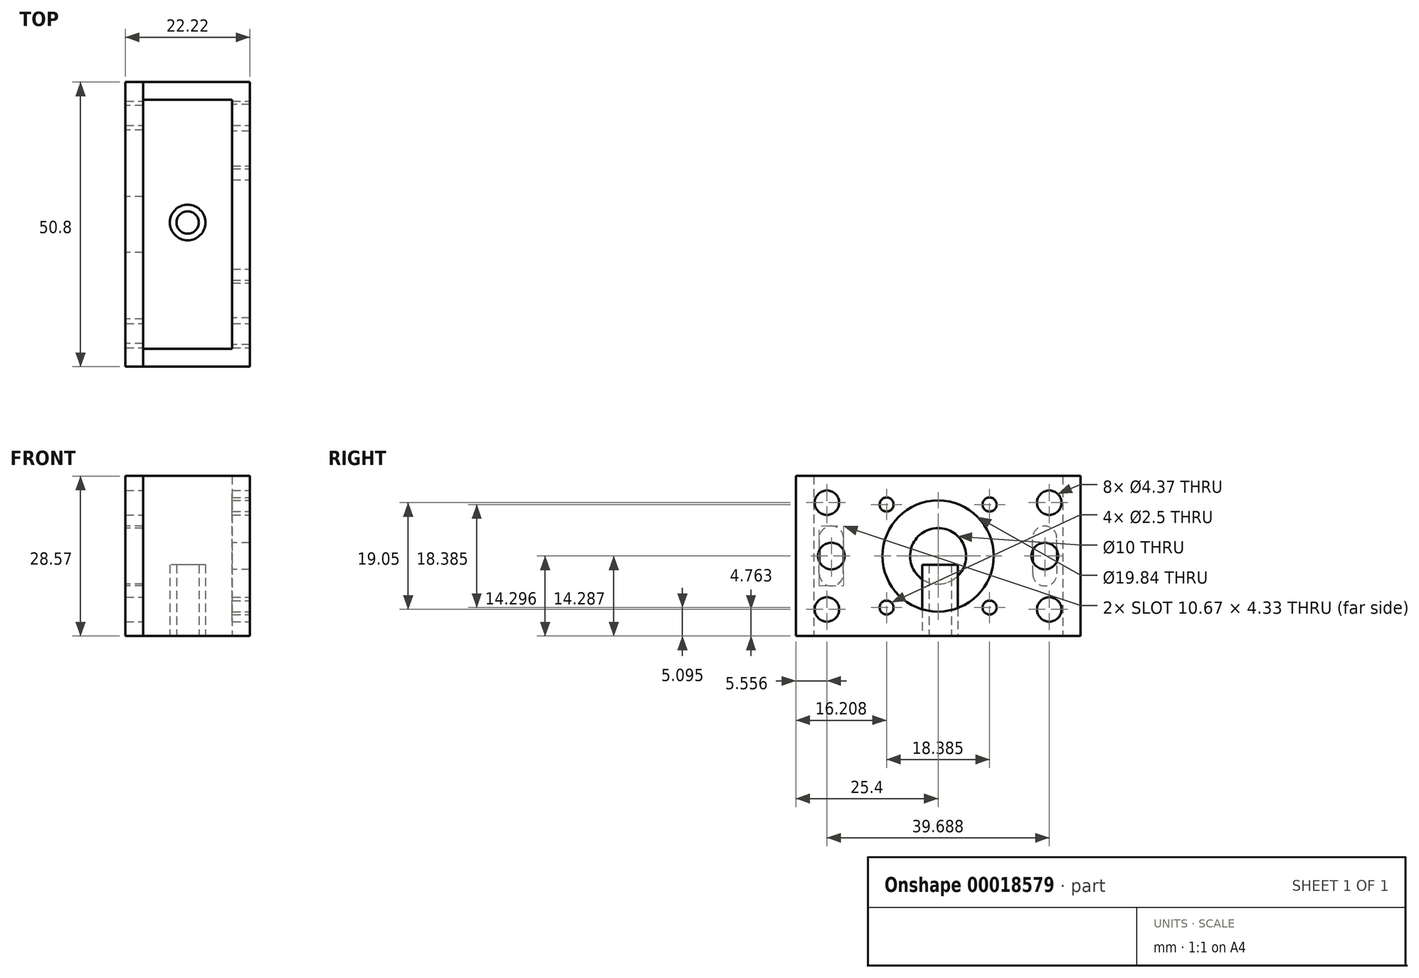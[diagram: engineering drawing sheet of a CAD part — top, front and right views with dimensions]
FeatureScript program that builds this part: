
annotation { "Feature Type Name" : "Feature", "Feature Type Description" : "" }
export const myFeature = defineFeature(function(context is Context, id is Id, definition is map)
    precondition{}
    {
        {
            var Q0;
            Q0=qCreatedBy(makeId("Top.planeOp"),FACE);
            var sketch = newSketch(context, id + "F0", { "sketchPlane" : qUnion([Q0])});
            skCircle(sketch, "E0", {"center": v(0, 0.35) * mm, "radius": 3.18 * mm});
            skCircle(sketch, "E1", {"center": v(0, 0.35) * mm, "radius": 2 * mm});
            skSolve(sketch);
        }
        {
            var Q0;
            Q0 = qSketchRegion(id + "F0", true);
            extrude(context, id + "F1", {"entities" : qUnion([Q0]), "depth" : 12.7 * mm});
        }
        {
            var Q0;
            Q0=qCreatedBy(makeId("Top.planeOp"),FACE);
            var sketch = newSketch(context, id + "F2", { "sketchPlane" : qUnion([Q0])});
            skLineSegment(sketch, "E2.rect.bottom", {"start": v(7.94, 22.22) * mm, "end": v(-7.94, 22.22) * mm});
            skLineSegment(sketch, "E2.rect.top", {"start": v(7.94, -22.22) * mm, "end": v(-7.94, -22.22) * mm});
            skLineSegment(sketch, "E2.rect.left", {"start": v(7.94, 22.22) * mm, "end": v(7.94, -22.23) * mm});
            skPoint(sketch, "E2.rect.middle", {"position": v(0, 0) * mm});
            skLineSegment(sketch, "E3.0", {"start": v(11.11, 25.4) * mm, "end": v(-7.94, 25.4) * mm});
            skLineSegment(sketch, "E3.1", {"start": v(11.11, 25.4) * mm, "end": v(11.11, -25.4) * mm});
            skLineSegment(sketch, "E3.2", {"start": v(11.11, -25.4) * mm, "end": v(-7.94, -25.4) * mm});
            skLineSegment(sketch, "E4", {"start": v(-7.94, 22.22) * mm, "end": v(-7.94, 25.4) * mm});
            skLineSegment(sketch, "E5", {"start": v(-7.94, -22.22) * mm, "end": v(-7.94, -25.4) * mm});
            skSolve(sketch);
        }
        {
            var Q0;
            Q0 = qSketchRegion(id + "F2", true);
            extrude(context, id + "F3", {"entities" : qUnion([Q0]), "depth" : 28.57 * mm});
        }
        {
            var Q0;
            Q0=makeQuery(id+"F3.opExtrude","SWEPT_FACE",FACE,{"disambiguationData":[OSD([sQuery(id+"F2.wireOp",EDGE,"E3.1")])]});
            var sketch = newSketch(context, id + "F4", { "sketchPlane" : qUnion([Q0])});
            skLineSegment(sketch, "E6", {"start": v(25.4, 14.29) * mm, "end": v(-25.4, 14.29) * mm, "construction": true});
            skLineSegment(sketch, "E7", {"start": v(0, 28.58) * mm, "end": v(0, 0) * mm, "construction": true});
            skCircle(sketch, "E8", {"center": v(0, 14.29) * mm, "radius": 9.92 * mm});
            skCircle(sketch, "E9", {"center": v(0, 14.29) * mm, "radius": 13 * mm, "construction": true});
            skCircle(sketch, "E10", {"center": v(9.2, 23.48) * mm, "radius": 1.25 * mm});
            skLineSegment(sketch, "E11", {"start": v(9.2, 23.48) * mm, "end": v(0, 14.29) * mm, "construction": true});
            skCircle(sketch, "E12.1.0", {"center": v(-9.2, 23.48) * mm, "radius": 1.25 * mm});
            skCircle(sketch, "E12.2.0", {"center": v(-9.2, 5.1) * mm, "radius": 1.25 * mm});
            skCircle(sketch, "E12.3.0", {"center": v(9.2, 5.1) * mm, "radius": 1.25 * mm});
            skSolve(sketch);
        }
        {
            var Q0;
            Q0 = qSketchRegion(id + "F4", true);
            extrude(context, id + "F5", {"entities" : qUnion([Q0]), "operationType" : NewBodyOperationType.REMOVE, "endBound" : BoundingType.UP_TO_NEXT, "oppositeDirection" : true, "depth" : 25 * mm});
        }
        {
            var Q0;
            Q0=qCreatedBy(makeId("Top.planeOp"),FACE);
            var sketch = newSketch(context, id + "F6", { "sketchPlane" : qUnion([Q0])});
            skLineSegment(sketch, "E13.bottom", {"start": v(-7.94, 25.4) * mm, "end": v(-11.11, 25.4) * mm});
            skLineSegment(sketch, "E13.top", {"start": v(-7.94, -25.4) * mm, "end": v(-11.11, -25.4) * mm});
            skLineSegment(sketch, "E13.left", {"start": v(-7.94, 25.4) * mm, "end": v(-7.94, -25.4) * mm});
            skLineSegment(sketch, "E13.right", {"start": v(-11.11, 25.4) * mm, "end": v(-11.11, -25.4) * mm});
            skSolve(sketch);
        }
        {
            var Q0;
            Q0 = qSketchRegion(id + "F6", true);
            var Q1;
            Q1=makeQuery(id+"F3.opExtrude","CAP_FACE",FACE,{"disambiguationData":[OSD([sQuery(id+"F2.wireOp",EDGE,"E2.rect.bottom"),sQuery(id+"F2.wireOp",EDGE,"E2.rect.top"),sQuery(id+"F2.wireOp",EDGE,"E2.rect.left"),sQuery(id+"F2.wireOp",EDGE,"E3.0"),sQuery(id+"F2.wireOp",EDGE,"E3.1"),sQuery(id+"F2.wireOp",EDGE,"E3.2"),sQuery(id+"F2.wireOp",EDGE,"E4"),sQuery(id+"F2.wireOp",EDGE,"E5")])],"isStart":false});
            extrude(context, id + "F7", {"entities" : qUnion([Q0]), "endBound" : BoundingType.UP_TO_SURFACE, "endBoundEntityFace" : qUnion([Q1]), "depth" : 25.4 * mm});
        }
        {
            var Q0;
            Q0=makeQuery(id+"F7.opExtrude","SWEPT_FACE",FACE,{"disambiguationData":[OSD([sQuery(id+"F6.wireOp",EDGE,"E13.right")])]});
            var sketch = newSketch(context, id + "F8", { "sketchPlane" : qUnion([Q0])});
            skCircle(sketch, "E14", {"center": v(0, 14.29) * mm, "radius": 5 * mm});
            skLineSegment(sketch, "E15", {"start": v(0, 28.57) * mm, "end": v(0, 0) * mm, "construction": true});
            skLineSegment(sketch, "E16", {"start": v(-25.4, 14.29) * mm, "end": v(25.4, 14.29) * mm, "construction": true});
            skSolve(sketch);
        }
        {
            var Q0;
            Q0 = qSketchRegion(id + "F8", true);
            extrude(context, id + "F9", {"entities" : qUnion([Q0]), "operationType" : NewBodyOperationType.REMOVE, "endBound" : BoundingType.UP_TO_NEXT, "oppositeDirection" : true, "depth" : 25.4 * mm});
        }
        {
            var Q0;
            Q0=makeQuery(id+"F3.opExtrude","SWEPT_FACE",FACE,{"disambiguationData":[OSD([sQuery(id+"F2.wireOp",EDGE,"E3.1")])]});
            var sketch = newSketch(context, id + "F10", { "sketchPlane" : qUnion([Q0])});
            skLineSegment(sketch, "E17", {"start": v(-19.84, 31.75) * mm, "end": v(-19.84, 0) * mm, "construction": true});
            skPoint(sketch, "E18", {"position": v(-19.84, 23.81) * mm});
            skLineSegment(sketch, "E19", {"start": v(0, 14.29) * mm, "end": v(-25.4, 14.29) * mm, "construction": true});
            skLineSegment(sketch, "E20", {"start": v(0, 14.29) * mm, "end": v(0, 28.57) * mm, "construction": true});
            skPoint(sketch, "E21.MirrorP", {"position": v(-19.84, 4.76) * mm});
            skPoint(sketch, "E22.MirrorP", {"position": v(19.84, 4.76) * mm});
            skPoint(sketch, "E23.MirrorP", {"position": v(19.84, 23.81) * mm});
            skSolve(sketch);
        }
        {
            var Q0;
            Q0=sQuery(id+"F10.wireOp",VERTEX,"E18");
            var Q1;
            Q1=sQuery(id+"F10.wireOp",VERTEX,"E23.MirrorP");
            var Q2;
            Q2=sQuery(id+"F10.wireOp",VERTEX,"E22.MirrorP");
            var Q3;
            Q3=sQuery(id+"F10.wireOp",VERTEX,"E21.MirrorP");
            var Q4;
            Q4=sQuery(id+"F10.wireOp",VERTEX,"7bfd8412-15d2-424a-8f3c-987d5bc530e7");
            var Q5;
            Q5=sQuery(id+"F10.wireOp",VERTEX,"433414ac-6cc2-401e-bdba-70e3e51737870.MirrorP");
            var Q6;
            Q6=makeQuery(id+"F3.opExtrude","SWEPT_BODY",BODY,{"disambiguationData":[OSD([sQuery(id+"F2.wireOp",EDGE,"E2.rect.bottom"),sQuery(id+"F2.wireOp",EDGE,"E2.rect.top"),sQuery(id+"F2.wireOp",EDGE,"E2.rect.left"),sQuery(id+"F2.wireOp",EDGE,"E3.0"),sQuery(id+"F2.wireOp",EDGE,"E3.1"),sQuery(id+"F2.wireOp",EDGE,"E3.2"),sQuery(id+"F2.wireOp",EDGE,"E4"),sQuery(id+"F2.wireOp",EDGE,"E5")])]});
            var Q7;
            Q7=makeQuery(id+"F7.opExtrude","SWEPT_BODY",BODY,{"disambiguationData":[OSD([sQuery(id+"F6.wireOp",EDGE,"E13.bottom"),sQuery(id+"F6.wireOp",EDGE,"E13.top"),sQuery(id+"F6.wireOp",EDGE,"E13.left"),sQuery(id+"F6.wireOp",EDGE,"E13.right")])]});
            hole(context, id + "F11", {"style" : HoleStyle.SIMPLE, "holeDiameter" : 4.37 * mm, "endStyle" : HoleEndStyle.THROUGH, "locations" : qUnion([Q0, Q1, Q2, Q3, Q4, Q5]), "scope" : qUnion([Q6, Q7])});
        }
        {
            var Q0;
            Q0=makeQuery(id+"F7.opExtrude","SWEPT_FACE",FACE,{"disambiguationData":[OSD([sQuery(id+"F6.wireOp",EDGE,"E13.right")])]});
            var sketch = newSketch(context, id + "F12", { "sketchPlane" : qUnion([Q0])});
            skLineSegment(sketch, "E24", {"start": v(-19.05, 26.06) * mm, "end": v(-19.05, 2.53) * mm, "construction": true});
            skLineSegment(sketch, "E25", {"start": v(0, 14.29) * mm, "end": v(0, 21.1) * mm, "construction": true});
            skLineSegment(sketch, "E26.rect.left", {"start": v(-16.9, 11.12) * mm, "end": v(-16.89, 17.47) * mm});
            skLineSegment(sketch, "E26.rect.right", {"start": v(-21.21, 11.12) * mm, "end": v(-21.2, 17.47) * mm});
            skPoint(sketch, "E26.rect.middle", {"position": v(-19.05, 14.3) * mm});
            skArc(sketch, "E27", {"start": v(-16.89, 17.47) * mm, "mid": v(-19.04, 19.63) * mm, "end": v(-21.2, 17.47) * mm});
            skArc(sketch, "E28", {"start": v(-21.21, 11.12) * mm, "mid": v(-19.06, 8.96) * mm, "end": v(-16.9, 11.12) * mm});
            skPoint(sketch, "E29.MirrorP", {"position": v(19.05, 14.3) * mm});
            skLineSegment(sketch, "E30.MirrorCS", {"start": v(21.21, 11.12) * mm, "end": v(21.2, 17.47) * mm});
            skArc(sketch, "E31.MirrorCS", {"start": v(21.21, 11.12) * mm, "mid": v(19.06, 8.96) * mm, "end": v(16.9, 11.12) * mm});
            skLineSegment(sketch, "E32.MirrorCS", {"start": v(16.9, 11.12) * mm, "end": v(16.89, 17.47) * mm});
            skArc(sketch, "E33.MirrorCS", {"start": v(16.89, 17.47) * mm, "mid": v(19.04, 19.63) * mm, "end": v(21.2, 17.47) * mm});
            skSolve(sketch);
        }
        {
            var Q0;
            Q0 = qSketchRegion(id + "F12", true);
            extrude(context, id + "F13", {"entities" : qUnion([Q0]), "operationType" : NewBodyOperationType.REMOVE, "endBound" : BoundingType.UP_TO_NEXT, "oppositeDirection" : true, "depth" : 25.4 * mm});
        }
        {
            var Q0;
            Q0=makeQuery(id+"F3.opExtrude","SWEPT_FACE",FACE,{"disambiguationData":[OSD([sQuery(id+"F2.wireOp",EDGE,"E2.rect.left")])]});
            var sketch = newSketch(context, id + "F14", { "sketchPlane" : qUnion([Q0])});
            skLineSegment(sketch, "E34", {"start": v(-21.2, 14.3) * mm, "end": v(-16.9, 14.3) * mm, "construction": true});
            skCircle(sketch, "E35", {"center": v(-19.05, 14.3) * mm, "radius": 2.38 * mm});
            skLineSegment(sketch, "E36", {"start": v(0, 0) * mm, "end": v(0, 28.58) * mm, "construction": true});
            skCircle(sketch, "E37.MirrorC", {"center": v(19.05, 14.3) * mm, "radius": 2.38 * mm});
            skSolve(sketch);
        }
        {
            var Q0;
            Q0 = qSketchRegion(id + "F14", true);
            extrude(context, id + "F15", {"entities" : qUnion([Q0]), "operationType" : NewBodyOperationType.REMOVE, "endBound" : BoundingType.UP_TO_NEXT, "oppositeDirection" : true, "depth" : 25 * mm});
        }
    });
